# Revit family: U-Stiel 3-seitig gelocht
name_source: partatom
category: Generic Models
revit_build: Autodesk Revit 2015 (Build: 20140606_1530(x64)
units: mm (PartAtom-declared; Revit-internal decimal feet)

## types (22) — shared parameters
Manufacturer = OBO Bettermann
Material = Steel, Galvanized
URL = http://www.obo-bettermann.com

## per-type parameters (varying)
| type | GTIN | Lenght | Manufacturer Art.No. |
| US 7 20 FT | 4012196187690 | 200 mm  [stored 0.656168 ft] | 6340016 |
| US 7 30 FT | 4012196187751 | 300 mm | 6340032 |
| US 7 40 FT | 4012196187812 | 400 mm  [stored 1.31234 ft] | 6340059 |
| US 7 50 FT | 4012196187874 | 500 mm  [stored 1.64042 ft] | 6340075 |
| US 7 60 FT | 4012196187935 | 600 mm | 6340091 |
| US 7 70 FT | 4012196187997 | 700 mm  [stored 2.29659 ft] | 6340113 |
| US 7 80 FT | 4012196188055 | 800 mm  [stored 2.62467 ft] | 6340148 |
| US 7 90 FT | 4012196188116 | 900 mm  [stored 2.95276 ft] | 6340164 |
| US 7 100 FT | 4012196188178 | 1000 mm  [stored 3.28084 ft] | 6340180 |
| US 7 110 FT | 4012196188239 | 1100 mm | 6340199 |
| US 7 120 FT | 4012196188291 | 1200 mm | 6340202 |
| US 7 130 FT | 4012196188352 | 1300 mm  [stored 4.26509 ft] | 6340210 |
| US 7 140 FT | 4012196188413 | 1400 mm  [stored 4.59318 ft] | 6340229 |
| US 7 150 FT | 4012196188475 | 1500 mm  [stored 4.92126 ft] | 6340237 |
| US 7 160 FT | 4012196188536 | 1600 mm  [stored 5.24934 ft] | 6340245 |
| US 7 170 FT | 4012196188598 | 1700 mm  [stored 5.57743 ft] | 6340253 |
| US 7 180 FT | 4012196188659 | 1800 mm  [stored 5.90551 ft] | 6340261 |
| US 7 190 FT | 4012196188710 | 1900 mm  [stored 6.2336 ft] | 6340288 |
| US 7 200 FT | 4012196188772 | 2000 mm  [stored 6.56168 ft] | 6340296 |
| US 7 300 FT | 4012196188895 | 3000 mm  [stored 9.84252 ft] | 6340377 |
| US 7 400 FT | 4012196458233 | 4000 mm  [stored 13.1234 ft] | 6340393 |
| US 7 600 FT | 4012196188833 | 6000 mm  [stored 19.685 ft] | 6340318 |

note: column(s) folded — value = type name in every type: Article Type

note: [stored X ft] marks values corroborated as IEEE doubles in the binary element streams (Revit-internal decimal feet)

## geometry (parser evidence)
native form markers: Sweep x4
no freeform markers — native parametric forms only
